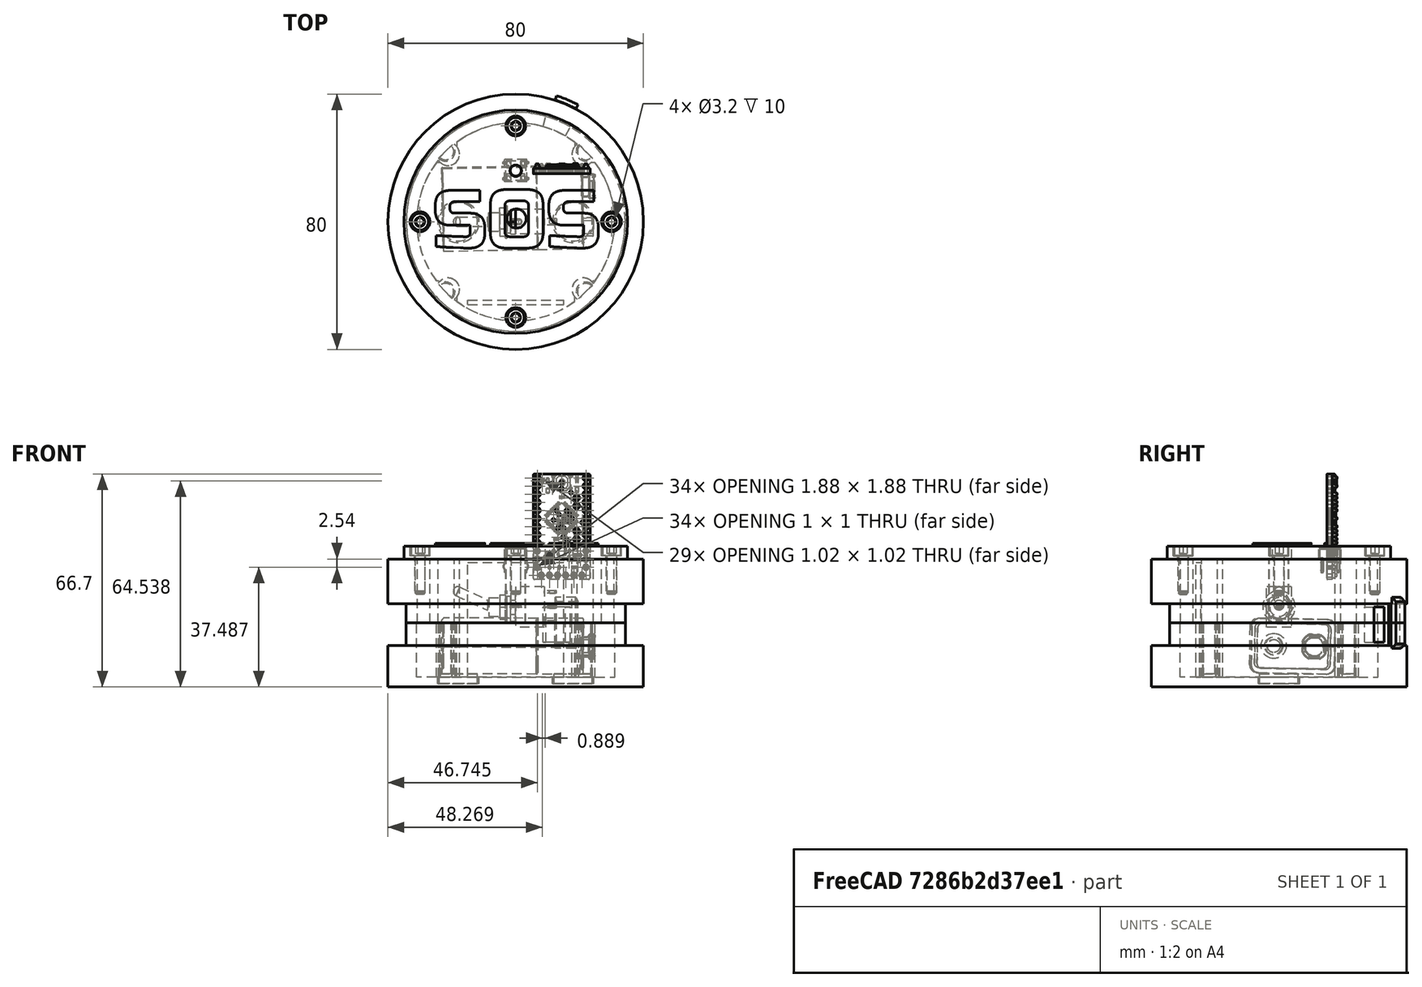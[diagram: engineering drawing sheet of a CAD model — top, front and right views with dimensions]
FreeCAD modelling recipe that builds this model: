
FCSTD DOCUMENT  (FreeCAD 0.17R12852 (Git))
Label: baliza_SOS_vial
License: All rights reserved
LicenseURL: http://es.wikipedia.org/wiki/Todos_los_derechos_reservados
objects: Part::Feature×162, Part::Cylinder×53, App::Part×20, Part::MultiFuse×18, Part::Cut×17, Part::Chamfer×7, Part::Box×2, App::DocumentObjectGroup×2, Part::Part2DObjectPython×1, Part::Extrusion×1, Part::Compound×1
note: 262 computed .brp shape members not serialized (recipe doc carries the construction recipe); baked Part::Feature solids carry a one-line shape summary decoded from their .brp

FEATURE [Part::Feature] Part__Feature  label="BAT 9v"
  Placement = pos=(65.8799,25.4256,-21.3482) rot=(-0.007455,0.009989,0.999922;1.58855rad)
  shape: bbox 48.07 x 27.42 x 18.05 mm, 192 faces (baked)
FEATURE [Part::Cylinder] Cylinder  label="exterior"
  Angle = 360
  AttacherType = Attacher::AttachEngine3D
  Height = 20
  Placement = pos=(0,0,-25) rot=(0,0,1;0rad)
  Radius = 40
FEATURE [Part::Cylinder] Cylinder001  label="vaciado"
  Angle = 360
  AttacherType = Attacher::AttachEngine3D
  Height = 20
  Placement = pos=(0,0,-22) rot=(0,0,1;0rad)
  Radius = 31
FEATURE [Part::Cylinder] Cylinder002  label="tira led exterior"
  Angle = 360
  AttacherType = Attacher::AttachEngine3D
  Height = 13
  Placement = pos=(0,0,-25) rot=(0,0,1;0rad)
  Radius = 41
FEATURE [Part::Cylinder] Cylinder003  label="tira led vaciado"
  Angle = 360
  AttacherType = Attacher::AttachEngine3D
  Height = 13
  Placement = pos=(0,0,-25) rot=(0,0,1;0rad)
  Radius = 34.3
FEATURE [Part::Cylinder] Cylinder004  label="orificio entrada cables sup"
  Angle = 14
  AttacherType = Attacher::AttachEngine3D
  Height = 11
  Placement = pos=(0,0,-11) rot=(0,0,1;1.0472rad)
  Radius = 35
FEATURE [Part::Chamfer] Chamfer001  label="M3 10mm004"
  Edges = 2 edges r=0.1: [Edge6,Edge7]
  Placement = pos=(0,-30,16) rot=(0,0,1;0rad)
FEATURE [Part::Cylinder] Cylinder010  label="torre tornillo003"
  Angle = 360
  AttacherType = Attacher::AttachEngine3D
  Height = 20
  Placement = pos=(0,-30,-25) rot=(0,0,1;0rad)
  Radius = 3.1
FEATURE [Part::Cylinder] Cylinder011  label="torre tornillo002"
  Angle = 360
  AttacherType = Attacher::AttachEngine3D
  Height = 20
  Placement = pos=(30,0,-25) rot=(0,0,1;0rad)
  Radius = 3.1
FEATURE [Part::Cylinder] Cylinder012  label="torre tornillo001"
  Angle = 360
  AttacherType = Attacher::AttachEngine3D
  Height = 20
  Placement = pos=(-30,0,-25) rot=(0,0,1;0rad)
  Radius = 3.1
FEATURE [Part::Cylinder] Cylinder013  label="torre tornillo"
  Angle = 360
  AttacherType = Attacher::AttachEngine3D
  Height = 20
  Placement = pos=(0,30,-25) rot=(0,0,1;0rad)
  Radius = 3.1
FEATURE [Part::Cylinder] Cylinder014  label="orificio tornillo"
  Angle = 360
  AttacherType = Attacher::AttachEngine3D
  Height = 10
  Placement = pos=(0,-30,5) rot=(0,0,1;0rad)
  Radius = 1.6
FEATURE [Part::Cylinder] Cylinder015  label="orificio tornillo001"
  Angle = 360
  AttacherType = Attacher::AttachEngine3D
  Height = 10
  Placement = pos=(-30,0,5) rot=(0,0,1;0rad)
  Radius = 1.6
FEATURE [Part::Cylinder] Cylinder016  label="orificio tornillo002"
  Angle = 360
  AttacherType = Attacher::AttachEngine3D
  Height = 10
  Placement = pos=(30,0,5) rot=(0,0,1;0rad)
  Radius = 1.6
FEATURE [Part::Cylinder] Cylinder017  label="orificio tornillo003"
  Angle = 360
  AttacherType = Attacher::AttachEngine3D
  Height = 10
  Placement = pos=(0,30,5) rot=(0,0,1;0rad)
  Radius = 1.6
FEATURE [Part::MultiFuse] Fusion  label="torres superiores"
  Placement = pos=(0,0,20) rot=(0,0,1;0rad)
  Shapes = -> [Cylinder010,Cylinder012,Cylinder013,Cylinder011]
FEATURE [Part::MultiFuse] Fusion017  label="orificios tornillos"
  Shapes = -> [Cylinder014,Cylinder016,Cylinder015,Cylinder017]
FEATURE [Part::Cylinder] Cylinder018  label="neodimio"
  Angle = 360
  AttacherType = Attacher::AttachEngine3D
  Height = 3
  Placement = pos=(18,0,-24) rot=(0,0,1;0.017453rad)
  Radius = 6
FEATURE [Part::Cylinder] Cylinder019  label="neodimio001"
  Angle = 360
  AttacherType = Attacher::AttachEngine3D
  Height = 3
  Placement = pos=(-18,0,-24) rot=(0,0,1;0.017453rad)
  Radius = 6
FEATURE [Part::Cylinder] Cylinder020  label="base neodimio002"
  Angle = 360
  AttacherType = Attacher::AttachEngine3D
  Height = 3
  Placement = pos=(18,0,-24) rot=(0,0,1;0.017453rad)
  Radius = 6.5
FEATURE [Part::Cylinder] Cylinder021  label="base neodimio003"
  Angle = 360
  AttacherType = Attacher::AttachEngine3D
  Height = 3
  Placement = pos=(-18,0,-24) rot=(0,0,1;0.017453rad)
  Radius = 6.5
FEATURE [Part::MultiFuse] Fusion018  label="bases neodimio"
  Shapes = -> [Cylinder020,Cylinder021]
FEATURE [Part::MultiFuse] Fusion019  label="Neodimios"
  Shapes = -> [Cylinder018,Cylinder019]
FEATURE [Part::Feature] Part__Feature001  label="Small Toggle Switch"
  shape: bbox 11.9 x 2.92 x 7.366 mm, 3 faces (baked)
FEATURE [Part::Feature] Part__Feature002  label="Small Toggle Switch001"
  shape: bbox 21.22 x 10.16 x 12.7 mm, 53 faces (baked)
FEATURE [App::Part] Small_Toggle_Switch
  Group = -> [Part__Feature001,Part__Feature002]
  License = CC BY 3.0
  LicenseURL = http://creativecommons.org/licenses/by/3.0/
  Origin = -> Origin
  Placement = pos=(0.25,1,17) rot=(0,1,0;1.5708rad)
FEATURE [Part::Cut] Cut  label="caja parte inferior"
  Base = -> Cylinder
  Tool = -> Cylinder001
FEATURE [Part::Cylinder] Cylinder027  label="exterior003"
  Angle = 360
  AttacherType = Attacher::AttachEngine3D
  Height = 20
  Placement = pos=(0,0,-25) rot=(0,0,1;0rad)
  Radius = 40
FEATURE [Part::Cylinder] Cylinder028  label="vaciado001"
  Angle = 360
  AttacherType = Attacher::AttachEngine3D
  Height = 20
  Placement = pos=(0,0,-25) rot=(0,0,1;0rad)
  Radius = 31
FEATURE [Part::Cut] Cut009  label="caja parte superior"
  Base = -> Cylinder027
  Placement = pos=(0,0,20) rot=(0,0,1;0rad)
  Tool = -> Cylinder028
FEATURE [Part::Cylinder] Cylinder029  label="torre fijacion001"
  Angle = 360
  AttacherType = Attacher::AttachEngine3D
  Height = 20
  Placement = pos=(0,-30,-25) rot=(0,0,1;0rad)
  Radius = 3.6
FEATURE [Part::Cylinder] Cylinder030  label="torre fijacion004"
  Angle = 360
  AttacherType = Attacher::AttachEngine3D
  Height = 20
  Placement = pos=(30,0,-25) rot=(0,0,1;0rad)
  Radius = 3.6
FEATURE [Part::Cylinder] Cylinder031  label="torre fijacion002"
  Angle = 360
  AttacherType = Attacher::AttachEngine3D
  Height = 20
  Placement = pos=(-30,0,-25) rot=(0,0,1;0rad)
  Radius = 3.6
FEATURE [Part::Cylinder] Cylinder032  label="torre fijacion003"
  Angle = 360
  AttacherType = Attacher::AttachEngine3D
  Height = 20
  Placement = pos=(0,30,-25) rot=(0,0,1;0rad)
  Radius = 3.6
FEATURE [Part::MultiFuse] Fusion023  label="torres inferiores"
  Placement = pos=(0,0,0) rot=(0,0,1;0.785398rad)
  Shapes = -> [Cylinder029,Cylinder031,Cylinder032,Cylinder030]
FEATURE [Part::Cut] Cut010  label="vaciado tira led inf"
  Base = -> Cylinder002
  Placement = pos=(0,0,13) rot=(0,0,1;0rad)
  Tool = -> Cylinder003
FEATURE [Part::Cylinder] Cylinder035  label="tira led exterior001"
  Angle = 360
  AttacherType = Attacher::AttachEngine3D
  Height = 13
  Placement = pos=(0,0,-25) rot=(0,0,1;0rad)
  Radius = 41
FEATURE [Part::Cylinder] Cylinder036  label="tira led vaciado001"
  Angle = 360
  AttacherType = Attacher::AttachEngine3D
  Height = 13
  Placement = pos=(0,0,-25) rot=(0,0,1;0rad)
  Radius = 34.3
FEATURE [Part::Cut] Cut013  label="vaciado tira led sup"
  Base = -> Cylinder035
  Placement = pos=(0,0,13) rot=(0,0,1;0rad)
  Tool = -> Cylinder036
FEATURE [Part::Cut] Cut014  label="caja parte superior001"
  Base = -> Cut009
  Tool = -> Cut013
FEATURE [Part::Cut] Cut015  label="caja parte inferior001"
  Base = -> Cut
  Tool = -> Cut010
FEATURE [Part::Cylinder] Cylinder037  label="vaciado fijacion001"
  Angle = 180
  AttacherType = Attacher::AttachEngine3D
  Height = 20
  Placement = pos=(0,-31,-25) rot=(0,0,1;0rad)
  Radius = 3
FEATURE [Part::Cylinder] Cylinder038  label="vaciado fijacion004"
  Angle = 180
  AttacherType = Attacher::AttachEngine3D
  Height = 20
  Placement = pos=(31.061,0.06103,-25) rot=(0,0,1;1.5708rad)
  Radius = 3
FEATURE [Part::Cylinder] Cylinder039  label="vaciado fijacion002"
  Angle = 180
  AttacherType = Attacher::AttachEngine3D
  Height = 20
  Placement = pos=(-31.0604,0.0980594,-25) rot=(0,0,-1;1.6057rad)
  Radius = 3
FEATURE [Part::Cylinder] Cylinder040  label="vaciado fijacion003"
  Angle = 180
  AttacherType = Attacher::AttachEngine3D
  Height = 20
  Placement = pos=(0,31.122,-25) rot=(0,0,1;-3.14159rad)
  Radius = 3
FEATURE [Part::MultiFuse] Fusion024  label="vaciado fijaciones"
  Placement = pos=(0,0,3) rot=(0,0,1;0.785398rad)
  Shapes = -> [Cylinder037,Cylinder039,Cylinder040,Cylinder038]
FEATURE [Part::Cylinder] Cylinder041  label="fijacion001"
  Angle = 180
  AttacherType = Attacher::AttachEngine3D
  Height = 20
  Placement = pos=(0,-31,-25) rot=(0,0,1;0rad)
  Radius = 2.6
FEATURE [Part::Cylinder] Cylinder042  label="fijacion002"
  Angle = 180
  AttacherType = Attacher::AttachEngine3D
  Height = 20
  Placement = pos=(-31.0604,0.0980594,-25) rot=(0,0,-1;1.6057rad)
  Radius = 2.6
FEATURE [Part::Cylinder] Cylinder043  label="fijacion003"
  Angle = 180
  AttacherType = Attacher::AttachEngine3D
  Height = 20
  Placement = pos=(0,31.122,-25) rot=(0,0,1;-3.14159rad)
  Radius = 2.6
FEATURE [Part::Cylinder] Cylinder044  label="fijacion004"
  Angle = 180
  AttacherType = Attacher::AttachEngine3D
  Height = 20
  Placement = pos=(31.061,0.06103,-25) rot=(0,0,1;1.5708rad)
  Radius = 2.6
FEATURE [Part::MultiFuse] Fusion025  label="fijaciones superior_inferior"
  Placement = pos=(0,0,4) rot=(0,0,1;0.785398rad)
  Shapes = -> [Cylinder041,Cylinder042,Cylinder043,Cylinder044]
FEATURE [Part::MultiFuse] Fusion026
  Shapes = -> [Cut015,Fusion023]
FEATURE [Part::Cut] Cut016  label="parte inferior"
  Base = -> Fusion026
  Tool = -> Fusion024
FEATURE [Part::Cylinder] Cylinder045  label="torre tornillo016"
  Angle = 360
  AttacherType = Attacher::AttachEngine3D
  Height = 20
  Placement = pos=(0,-30,-25) rot=(0,0,1;0rad)
  Radius = 3.6
FEATURE [Part::Cylinder] Cylinder046  label="torre tornillo017"
  Angle = 360
  AttacherType = Attacher::AttachEngine3D
  Height = 20
  Placement = pos=(30,0,-25) rot=(0,0,1;0rad)
  Radius = 3.6
FEATURE [Part::Cylinder] Cylinder047  label="torre tornillo018"
  Angle = 360
  AttacherType = Attacher::AttachEngine3D
  Height = 20
  Placement = pos=(-30,0,-25) rot=(0,0,1;0rad)
  Radius = 3.6
FEATURE [Part::Cylinder] Cylinder048  label="torre tornillo019"
  Angle = 360
  AttacherType = Attacher::AttachEngine3D
  Height = 20
  Placement = pos=(0,30,-25) rot=(0,0,1;0rad)
  Radius = 3.6
FEATURE [Part::MultiFuse] Fusion027  label="torres superiores001"
  Placement = pos=(0,0,20) rot=(0,0,1;0.785398rad)
  Shapes = -> [Cylinder045,Cylinder047,Cylinder048,Cylinder046]
FEATURE [Part::MultiFuse] Fusion028
  Shapes = -> [Cut014,Fusion027]
FEATURE [Part::MultiFuse] Fusion029  label="parte superior fijaciones inferiores"
  Shapes = -> [Fusion025,Fusion028]
FEATURE [Part::MultiFuse] Fusion030
  Shapes = -> [Fusion,Fusion029]
FEATURE [Part::Cut] Cut017  label="parte superior"
  Base = -> Fusion030
  Tool = -> Fusion017
FEATURE [Part::Cut] Cut018  label="parte inferior001"
  Base = -> Cut016
  Tool = -> Fusion018
FEATURE [Part::Cylinder] Cylinder049  label="orificio entrada cables inf"
  Angle = 14
  AttacherType = Attacher::AttachEngine3D
  Height = 11
  Placement = pos=(0,0,-11) rot=(0,0,1;1.0472rad)
  Radius = 35
FEATURE [Part::Cut] Cut019  label="parte inferior v1"
  Base = -> Cut018
  Tool = -> Cylinder049
FEATURE [Part::Cut] Cut020  label="parte superior001"
  Base = -> Cut017
  Tool = -> Cylinder004
FEATURE [Part::Cylinder] Cylinder052  label="tapa superior"
  Angle = 360
  AttacherType = Attacher::AttachEngine3D
  Height = 4
  Placement = pos=(0,0,15) rot=(0,0,1;0rad)
  Radius = 35
FEATURE [Part::Cylinder] Cylinder053  label="entrada tornillo004"
  Angle = 360
  AttacherType = Attacher::AttachEngine3D
  Height = 3
  Placement = pos=(0,-30,16) rot=(0,0,1;0rad)
  Radius = 3.1
FEATURE [Part::Cylinder] Cylinder054  label="entrada tornillo005"
  Angle = 360
  AttacherType = Attacher::AttachEngine3D
  Height = 3
  Placement = pos=(0,30,16) rot=(0,0,1;0rad)
  Radius = 3.1
FEATURE [Part::Cylinder] Cylinder055  label="entrada tornillo006"
  Angle = 360
  AttacherType = Attacher::AttachEngine3D
  Height = 3
  Placement = pos=(30,0,16) rot=(0,0,1;0rad)
  Radius = 3.1
FEATURE [Part::Cylinder] Cylinder056  label="entrada tornillo007"
  Angle = 360
  AttacherType = Attacher::AttachEngine3D
  Height = 3
  Placement = pos=(-30,0,16) rot=(0,0,1;0rad)
  Radius = 3.1
FEATURE [Part::MultiFuse] Fusion036  label="vaciados cabeza tornillos001"
  Shapes = -> [Cylinder053,Cylinder055,Cylinder056,Cylinder054]
FEATURE [Part::Cut] Cut006
  Base = -> Cylinder052
  Tool = -> Fusion036
FEATURE [Part::Cylinder] Cylinder057  label="orificio tornillo008"
  Angle = 360
  AttacherType = Attacher::AttachEngine3D
  Height = 10
  Placement = pos=(0,-30,5) rot=(0,0,1;0rad)
  Radius = 1.7
FEATURE [Part::Cylinder] Cylinder058  label="orificio tornillo009"
  Angle = 360
  AttacherType = Attacher::AttachEngine3D
  Height = 10
  Placement = pos=(30,0,5) rot=(0,0,1;0rad)
  Radius = 1.7
FEATURE [Part::Cylinder] Cylinder059  label="orificio tornillo010"
  Angle = 360
  AttacherType = Attacher::AttachEngine3D
  Height = 10
  Placement = pos=(-30,0,5) rot=(0,0,1;0rad)
  Radius = 1.7
FEATURE [Part::Cylinder] Cylinder060  label="orificio tornillo011"
  Angle = 360
  AttacherType = Attacher::AttachEngine3D
  Height = 10
  Placement = pos=(0,30,5) rot=(0,0,1;0rad)
  Radius = 1.7
FEATURE [Part::MultiFuse] Fusion037  label="orificios tornillos002"
  Placement = pos=(0,0,3) rot=(0,0,1;0rad)
  Shapes = -> [Cylinder057,Cylinder058,Cylinder059,Cylinder060]
FEATURE [Part::Cut] Cut007  label="tapa superior001"
  Base = -> Cut006
  Tool = -> Fusion037
FEATURE [Part::Part2DObjectPython] ShapeString001  # Draft 2D object (typed FeaturePython)
  FontFile = <userpath>/Descargas/Russo_One/RussoOne-Regular.ttf
  Placement = pos=(-26,-8,19) rot=(0,0,1;0rad)
  Size = 10
  String = SOS
  Tracking = 0
FEATURE [Part::Extrusion] Extrude002
  Base = -> ShapeString001
  Dir = (0,0,1)
  DirMode = 2
  FaceMakerClass = Part::FaceMakerBullseye
  LengthFwd = 1
  LengthRev = 0
  Solid = true
  Symmetric = false
FEATURE [Part::MultiFuse] Fusion022  label="tapa"
  Shapes = -> [Extrude002,Cut007]
FEATURE [Part::Cylinder] Cylinder061  label="Cilindro001"
  Angle = 360
  AttacherType = Attacher::AttachEngine3D
  Height = 10
  Placement = pos=(0.25,1,11) rot=(0,0,1;0rad)
  Radius = 3
FEATURE [Part::Cut] Cut008  label="tapa interruptor sin pushbutton"
  Base = -> Fusion022
  Tool = -> Cylinder061
FEATURE [Part::Feature] Part__Feature003  label="board"
  Placement = pos=(5.47521,15.0552,41.6975) rot=(0,0,1;0rad)
  shape: bbox 17.85 x 1.67 x 33.09 mm, 530 faces (baked)
FEATURE [Part::Feature] Part__Feature004  label="ATmega"
  Placement = pos=(14.3652,16.8027,27.7275) rot=(0,-1,0;0.785398rad)
  shape: bbox 10.57 x 1.099 x 10.57 mm, 1762 faces (baked)
FEATURE [Part::Feature] Part__Feature005  label="cap_603"
  Placement = pos=(10.3417,16.7052,40.4401) rot=(0,1,0;1.5708rad)
  shape: bbox 0.8 x 0.8 x 0.4 mm, 18 faces (baked)
FEATURE [Part::Feature] Part__Feature006  label="cap_604"
  Placement = pos=(10.3417,16.7052,40.4401) rot=(0,1,0;1.5708rad)
  shape: bbox 0.8 x 0.8 x 0.4 mm, 18 faces (baked)
FEATURE [Part::Feature] Part__Feature007  label="cap_605"
  Placement = pos=(10.3417,16.7052,40.4401) rot=(0,1,0;1.5708rad)
  shape: bbox 0.8 x 0.8 x 0.8 mm, 10 faces (baked)
FEATURE [App::Part] cap_603  label="cap_606"
  Group = -> [Part__Feature005,Part__Feature006,Part__Feature007]
  License = CC BY 3.0
  LicenseURL = http://creativecommons.org/licenses/by/3.0/
  Origin = -> Origin001
FEATURE [Part::Feature] Part__Feature008  label="cap_607"
  Placement = pos=(13.6922,16.7052,34.8585) rot=(0,0,1;0rad)
  shape: bbox 0.4 x 0.8 x 0.8 mm, 18 faces (baked)
FEATURE [Part::Feature] Part__Feature009  label="cap_608"
  Placement = pos=(13.6922,16.7052,34.8585) rot=(0,0,1;0rad)
  shape: bbox 0.4 x 0.8 x 0.8 mm, 18 faces (baked)
FEATURE [Part::Feature] Part__Feature010  label="cap_609"
  Placement = pos=(13.6922,16.7052,34.8585) rot=(0,0,1;0rad)
  shape: bbox 0.8 x 0.8 x 0.8 mm, 10 faces (baked)
FEATURE [App::Part] cap_603001
  Group = -> [Part__Feature008,Part__Feature009,Part__Feature010]
  License = CC BY 3.0
  LicenseURL = http://creativecommons.org/licenses/by/3.0/
  Origin = -> Origin002
FEATURE [Part::Feature] Part__Feature011  label="cap_603002"
  Placement = pos=(11.8634,16.7052,21.6759) rot=(0,0,1;0rad)
  shape: bbox 0.4 x 0.8 x 0.8 mm, 18 faces (baked)
FEATURE [Part::Feature] Part__Feature012  label="cap_603003"
  Placement = pos=(11.8634,16.7052,21.6759) rot=(0,0,1;0rad)
  shape: bbox 0.4 x 0.8 x 0.8 mm, 18 faces (baked)
FEATURE [Part::Feature] Part__Feature013  label="cap_603004"
  Placement = pos=(11.8634,16.7052,21.6759) rot=(0,0,1;0rad)
  shape: bbox 0.8 x 0.8 x 0.8 mm, 10 faces (baked)
FEATURE [App::Part] cap_603002  label="cap_603005"
  Group = -> [Part__Feature011,Part__Feature012,Part__Feature013]
  License = CC BY 3.0
  LicenseURL = http://creativecommons.org/licenses/by/3.0/
  Origin = -> Origin003
FEATURE [Part::Feature] Part__Feature014  label="cap_603006"
  Placement = pos=(17.4768,16.7052,12.8875) rot=(0,0,1;0rad)
  shape: bbox 0.4 x 0.8 x 0.8 mm, 18 faces (baked)
FEATURE [Part::Feature] Part__Feature015  label="cap_603007"
  Placement = pos=(17.4768,16.7052,12.8875) rot=(0,0,1;0rad)
  shape: bbox 0.4 x 0.8 x 0.8 mm, 18 faces (baked)
FEATURE [Part::Feature] Part__Feature016  label="cap_603008"
  Placement = pos=(17.4768,16.7052,12.8875) rot=(0,0,1;0rad)
  shape: bbox 0.8 x 0.8 x 0.8 mm, 10 faces (baked)
FEATURE [App::Part] cap_603003  label="cap_603009"
  Group = -> [Part__Feature014,Part__Feature015,Part__Feature016]
  License = CC BY 3.0
  LicenseURL = http://creativecommons.org/licenses/by/3.0/
  Origin = -> Origin004
FEATURE [Part::Feature] Part__Feature017  label="res_603"
  Placement = pos=(10.4218,16.7052,37.2651) rot=(0,1,0;1.5708rad)
  shape: bbox 0.8 x 0.5 x 0.3 mm, 18 faces (baked)
FEATURE [Part::Feature] Part__Feature018  label="res_604"
  Placement = pos=(10.4218,16.7052,37.2651) rot=(0,1,0;1.5708rad)
  shape: bbox 0.8 x 0.5 x 0.3 mm, 18 faces (baked)
FEATURE [Part::Feature] Part__Feature019  label="res_605"
  Placement = pos=(10.4218,16.7052,37.2651) rot=(0,1,0;1.5708rad)
  shape: bbox 0.8 x 0.5 x 1 mm, 10 faces (baked)
FEATURE [App::Part] res_603  label="res_606"
  Group = -> [Part__Feature017,Part__Feature018,Part__Feature019]
  License = CC BY 3.0
  LicenseURL = http://creativecommons.org/licenses/by/3.0/
  Origin = -> Origin005
FEATURE [Part::Feature] Part__Feature020  label="res_607"
  Placement = pos=(19.5912,16.7052,37.5953) rot=(0,1,0;1.5708rad)
  shape: bbox 0.8 x 0.5 x 0.3 mm, 18 faces (baked)
FEATURE [Part::Feature] Part__Feature021  label="res_608"
  Placement = pos=(19.5912,16.7052,37.5953) rot=(0,1,0;1.5708rad)
  shape: bbox 0.8 x 0.5 x 0.3 mm, 18 faces (baked)
FEATURE [Part::Feature] Part__Feature022  label="res_609"
  Placement = pos=(19.5912,16.7052,37.5953) rot=(0,1,0;1.5708rad)
  shape: bbox 0.8 x 0.5 x 1 mm, 10 faces (baked)
FEATURE [App::Part] res_603001
  Group = -> [Part__Feature020,Part__Feature021,Part__Feature022]
  License = CC BY 3.0
  LicenseURL = http://creativecommons.org/licenses/by/3.0/
  Origin = -> Origin006
FEATURE [Part::Feature] Part__Feature023  label="res_603002"
  Placement = pos=(15.1652,16.7052,14.6275) rot=(0,1,0;-3.14159rad)
  shape: bbox 0.3 x 0.5 x 0.8 mm, 18 faces (baked)
FEATURE [Part::Feature] Part__Feature024  label="res_603003"
  Placement = pos=(15.1652,16.7052,14.6275) rot=(0,1,0;-3.14159rad)
  shape: bbox 0.3 x 0.5 x 0.8 mm, 18 faces (baked)
FEATURE [Part::Feature] Part__Feature025  label="res_603004"
  Placement = pos=(15.1652,16.7052,14.6275) rot=(0,1,0;-3.14159rad)
  shape: bbox 1 x 0.5 x 0.8 mm, 10 faces (baked)
FEATURE [App::Part] res_603002  label="res_603005"
  Group = -> [Part__Feature023,Part__Feature024,Part__Feature025]
  License = CC BY 3.0
  LicenseURL = http://creativecommons.org/licenses/by/3.0/
  Origin = -> Origin007
FEATURE [Part::Feature] Part__Feature026  label="condensateurTantale_106C_Dfaut"
  Placement = pos=(10.1742,17.5052,15.6625) rot=(0,1,0;1.5708rad)
  shape: bbox 1.2 x 0.8101 x 0.6565 mm, 50 faces (baked)
FEATURE [Part::Feature] Part__Feature027  label="condensateurTantale_106C_Dfaut001"
  Placement = pos=(10.1742,17.5052,15.6625) rot=(0,1,0;1.5708rad)
  shape: bbox 1.2 x 0.8101 x 0.6565 mm, 50 faces (baked)
FEATURE [Part::Feature] Part__Feature028  label="condensateurTantale_106C_Dfaut002"
  Placement = pos=(10.1742,17.5052,15.6625) rot=(0,1,0;1.5708rad)
  shape: bbox 1.6 x 1.551 x 3.187 mm, 88 faces (baked)
FEATURE [App::Part] condensateurTantale_106C_D__faut
  Group = -> [Part__Feature026,Part__Feature027,Part__Feature028]
  License = CC BY 3.0
  LicenseURL = http://creativecommons.org/licenses/by/3.0/
  Origin = -> Origin008
FEATURE [Part::Feature] Part__Feature029  label="condensateurTantale_106C_Dfaut003"
  Placement = pos=(18.6832,17.5052,17.5675) rot=(0,1,0;1.5708rad)
  shape: bbox 1.2 x 0.8101 x 0.6565 mm, 50 faces (baked)
FEATURE [Part::Feature] Part__Feature030  label="condensateurTantale_106C_Dfaut004"
  Placement = pos=(18.6832,17.5052,17.5675) rot=(0,1,0;1.5708rad)
  shape: bbox 1.2 x 0.8101 x 0.6565 mm, 50 faces (baked)
FEATURE [Part::Feature] Part__Feature031  label="condensateurTantale_106C_Dfaut005"
  Placement = pos=(18.6832,17.5052,17.5675) rot=(0,1,0;1.5708rad)
  shape: bbox 1.6 x 1.551 x 3.187 mm, 88 faces (baked)
FEATURE [App::Part] condensateurTantale_106C_D__faut001
  Group = -> [Part__Feature029,Part__Feature030,Part__Feature031]
  License = CC BY 3.0
  LicenseURL = http://creativecommons.org/licenses/by/3.0/
  Origin = -> Origin009
FEATURE [Part::Feature] Part__Feature032  label="SOT23-5"
  Placement = pos=(14.3653,16.6848,17.5167) rot=(-1,0,0;1.5708rad)
  shape: bbox 0.6498 x 0.8924 x 0.5 mm, 7 faces (baked)
FEATURE [Part::Feature] Part__Feature033  label="SOT23-006"
  Placement = pos=(14.3653,16.6848,17.5167) rot=(-1,0,0;1.5708rad)
  shape: bbox 1.823 x 2.71 x 3.209 mm, 34 faces (baked)
FEATURE [Part::Feature] Part__Feature034  label="SOT23-007"
  Placement = pos=(14.3653,16.6848,17.5167) rot=(-1,0,0;1.5708rad)
  shape: bbox 0.6498 x 0.8924 x 0.5 mm, 7 faces (baked)
FEATURE [Part::Feature] Part__Feature035  label="SOT23-008"
  Placement = pos=(14.3653,16.6848,17.5167) rot=(-1,0,0;1.5708rad)
  shape: bbox 0.6498 x 0.8924 x 0.5 mm, 7 faces (baked)
FEATURE [Part::Feature] Part__Feature036  label="SOT23-009"
  Placement = pos=(14.3653,16.6848,17.5167) rot=(-1,0,0;1.5708rad)
  shape: bbox 0.6498 x 0.8924 x 0.5 mm, 7 faces (baked)
FEATURE [Part::Feature] Part__Feature037  label="SOT23-010"
  Placement = pos=(14.3653,16.6848,17.5167) rot=(-1,0,0;1.5708rad)
  shape: bbox 0.6498 x 0.8924 x 0.5 mm, 7 faces (baked)
FEATURE [App::Part] SOT23_5
  Group = -> [Part__Feature032,Part__Feature033,Part__Feature034,Part__Feature035,Part__Feature036,Part__Feature037]
  License = CC BY 3.0
  LicenseURL = http://creativecommons.org/licenses/by/3.0/
  Origin = -> Origin010
FEATURE [Part::Feature] Part__Feature038  label="Surface Mount Chip LED 3.2x1.6mm"
  Placement = pos=(18.7112,16.7112,39.0103) rot=(0.57735,0.57735,0.57735;-2.0944rad)
  shape: bbox 0.96 x 0.006 x 0.24 mm, 10 faces (baked)
FEATURE [Part::Feature] Part__Feature039  label="Surface Mount Chip LED 3.2x1.6mm001"
  Placement = pos=(18.7112,16.7112,39.0103) rot=(0.57735,0.57735,0.57735;-2.0944rad)
  shape: bbox 0.72 x 0.312 x 0.36 mm, 15 faces (baked)
FEATURE [Part::Feature] Part__Feature040  label="Surface Mount Chip LED 3.2x1.6mm002"
  Placement = pos=(18.7112,16.7112,39.0103) rot=(0.57735,0.57735,0.57735;-2.0944rad)
  shape: bbox 0.96 x 0.3661 x 1.2 mm, 24 faces (baked)
FEATURE [Part::Feature] Part__Feature041  label="Surface Mount Chip LED 3.2x1.6mm003"
  Placement = pos=(18.7112,16.7112,39.0103) rot=(0.57735,0.57735,0.57735;-2.0944rad)
  shape: bbox 0.72 x 0.312 x 0.36 mm, 17 faces (baked)
FEATURE [Part::Feature] Part__Feature042  label="Surface Mount Chip LED 3.2x1.6mm004"
  Placement = pos=(18.7112,16.7112,39.0103) rot=(0.57735,0.57735,0.57735;-2.0944rad)
  shape: bbox 0.984 x 0.36 x 1.944 mm, 79 faces (baked)
FEATURE [Part::Feature] Part__Feature043  label="Surface Mount Chip LED 3.2x1.6mm005"
  Placement = pos=(18.7112,16.7112,39.0103) rot=(0.57735,0.57735,0.57735;-2.0944rad)
  shape: bbox 0.12 x 0.006 x 0.12 mm, 6 faces (baked)
FEATURE [Part::Feature] Part__Feature044  label="Surface Mount Chip LED 3.2x1.6mm006"
  Placement = pos=(18.7112,16.7112,39.0103) rot=(0.57735,0.57735,0.57735;-2.0944rad)
  shape: bbox 0.12 x 0.006 x 0.12 mm, 6 faces (baked)
FEATURE [App::Part] Surface_Mount_Chip_LED_3_2x1_6mm
  Group = -> [Part__Feature038,Part__Feature039,Part__Feature040,Part__Feature041,Part__Feature042,Part__Feature043,Part__Feature044]
  License = CC BY 3.0
  LicenseURL = http://creativecommons.org/licenses/by/3.0/
  Origin = -> Origin011
FEATURE [Part::Feature] Part__Feature045  label="Surface Mount Chip LED 3.2x1.6mm007"
  Placement = pos=(13.4306,16.7112,20.3081) rot=(-1,0,0;1.5708rad)
  shape: bbox 0.24 x 0.006 x 0.96 mm, 10 faces (baked)
FEATURE [Part::Feature] Part__Feature046  label="Surface Mount Chip LED 3.2x1.6mm008"
  Placement = pos=(13.4306,16.7112,20.3081) rot=(-1,0,0;1.5708rad)
  shape: bbox 0.36 x 0.312 x 0.72 mm, 15 faces (baked)
FEATURE [Part::Feature] Part__Feature047  label="Surface Mount Chip LED 3.2x1.6mm009"
  Placement = pos=(13.4306,16.7112,20.3081) rot=(-1,0,0;1.5708rad)
  shape: bbox 1.2 x 0.3661 x 0.96 mm, 24 faces (baked)
FEATURE [Part::Feature] Part__Feature048  label="Surface Mount Chip LED 3.2x1.6mm010"
  Placement = pos=(13.4306,16.7112,20.3081) rot=(-1,0,0;1.5708rad)
  shape: bbox 0.36 x 0.312 x 0.72 mm, 17 faces (baked)
FEATURE [Part::Feature] Part__Feature049  label="Surface Mount Chip LED 3.2x1.6mm011"
  Placement = pos=(13.4306,16.7112,20.3081) rot=(-1,0,0;1.5708rad)
  shape: bbox 1.944 x 0.36 x 0.984 mm, 79 faces (baked)
FEATURE [Part::Feature] Part__Feature050  label="Surface Mount Chip LED 3.2x1.6mm012"
  Placement = pos=(13.4306,16.7112,20.3081) rot=(-1,0,0;1.5708rad)
  shape: bbox 0.12 x 0.006 x 0.12 mm, 6 faces (baked)
FEATURE [Part::Feature] Part__Feature051  label="Surface Mount Chip LED 3.2x1.6mm013"
  Placement = pos=(13.4306,16.7112,20.3081) rot=(-1,0,0;1.5708rad)
  shape: bbox 0.12 x 0.006 x 0.12 mm, 6 faces (baked)
FEATURE [App::Part] Surface_Mount_Chip_LED_3_2x1_6mm001
  Group = -> [Part__Feature045,Part__Feature046,Part__Feature047,Part__Feature048,Part__Feature049,Part__Feature050,Part__Feature051]
  License = CC BY 3.0
  LicenseURL = http://creativecommons.org/licenses/by/3.0/
  Origin = -> Origin012
FEATURE [Part::Feature] Part__Feature052  label="Fusion001"
  shape: bbox 5.215 x 3.028 x 0.825 mm, 41 faces (baked)
FEATURE [App::Part] Crystal_Low_Profile
  Group = -> [Part__Feature052]
  License = CC BY 3.0
  LicenseURL = http://creativecommons.org/licenses/by/3.0/
  Origin = -> Origin013
  Placement = pos=(9.71701,16.7052,22.6754) rot=(-0.57735,0.57735,0.57735;2.0944rad)
FEATURE [Part::Feature] Part__Feature053  label="TACTILE-SWITCH-SMD-ALT01"
  Placement = pos=(14.4922,16.7052,39.0305) rot=(0,0,1;0rad)
  shape: bbox 6.4 x 1.404 x 5.219 mm, 156 faces (baked)
FEATURE [Part::Feature] Part__Feature054  label="Pin Header 1x12 TH Pitch 2.54mm"
  Placement = pos=(6.74521,15.0555,40.428) rot=(0.577364,0.577364,-0.577322;2.09444rad)
  shape: bbox 0.63 x 12.7 x 0.6305 mm, 14 faces, 0 solids (baked)
FEATURE [Part::Feature] Part__Feature055  label="Pin Header 1x12 TH Pitch 2.54mm001"
  Placement = pos=(6.74521,15.0555,40.428) rot=(0.577364,0.577364,-0.577322;2.09444rad)
  shape: bbox 0.63 x 12.7 x 0.6305 mm, 14 faces, 0 solids (baked)
FEATURE [Part::Feature] Part__Feature056  label="Pin Header 1x12 TH Pitch 2.54mm002"
  Placement = pos=(6.74521,15.0555,40.428) rot=(0.577364,0.577364,-0.577322;2.09444rad)
  shape: bbox 0.63 x 12.7 x 0.6305 mm, 14 faces, 0 solids (baked)
FEATURE [Part::Feature] Part__Feature057  label="Pin Header 1x12 TH Pitch 2.54mm003"
  Placement = pos=(6.74521,15.0555,40.428) rot=(0.577364,0.577364,-0.577322;2.09444rad)
  shape: bbox 0.63 x 12.7 x 0.6305 mm, 14 faces, 0 solids (baked)
FEATURE [Part::Feature] Part__Feature058  label="Pin Header 1x12 TH Pitch 2.54mm004"
  Placement = pos=(6.74521,15.0555,40.428) rot=(0.577364,0.577364,-0.577322;2.09444rad)
  shape: bbox 0.63 x 12.7 x 0.6305 mm, 14 faces, 0 solids (baked)
FEATURE [Part::Feature] Part__Feature059  label="Pin Header 1x12 TH Pitch 2.54mm005"
  Placement = pos=(6.74521,15.0555,40.428) rot=(0.577364,0.577364,-0.577322;2.09444rad)
  shape: bbox 0.63 x 12.7 x 0.6305 mm, 14 faces, 0 solids (baked)
FEATURE [Part::Feature] Part__Feature060  label="Pin Header 1x12 TH Pitch 2.54mm006"
  Placement = pos=(6.74521,15.0555,40.428) rot=(0.577364,0.577364,-0.577322;2.09444rad)
  shape: bbox 0.63 x 12.7 x 0.6305 mm, 14 faces, 0 solids (baked)
FEATURE [Part::Feature] Part__Feature061  label="Pin Header 1x12 TH Pitch 2.54mm007"
  Placement = pos=(6.74521,15.0555,40.428) rot=(0.577364,0.577364,-0.577322;2.09444rad)
  shape: bbox 0.63 x 12.7 x 0.6305 mm, 14 faces, 0 solids (baked)
FEATURE [Part::Feature] Part__Feature062  label="Pin Header 1x12 TH Pitch 2.54mm008"
  Placement = pos=(6.74521,15.0555,40.428) rot=(0.577364,0.577364,-0.577322;2.09444rad)
  shape: bbox 0.63 x 12.7 x 0.6305 mm, 14 faces, 0 solids (baked)
FEATURE [Part::Feature] Part__Feature063  label="Pin Header 1x12 TH Pitch 2.54mm009"
  Placement = pos=(6.74521,15.0555,40.428) rot=(0.577364,0.577364,-0.577322;2.09444rad)
  shape: bbox 0.63 x 12.7 x 0.6305 mm, 14 faces, 0 solids (baked)
FEATURE [Part::Feature] Part__Feature064  label="Pin Header 1x12 TH Pitch 2.54mm010"
  Placement = pos=(6.74521,15.0555,40.428) rot=(0.577364,0.577364,-0.577322;2.09444rad)
  shape: bbox 0.63 x 12.7 x 0.6305 mm, 14 faces, 0 solids (baked)
FEATURE [Part::Feature] Part__Feature065  label="Pin Header 1x12 TH Pitch 2.54mm011"
  Placement = pos=(6.74521,15.0555,40.428) rot=(0.577364,0.577364,-0.577322;2.09444rad)
  shape: bbox 0.63 x 12.7 x 0.6305 mm, 14 faces, 0 solids (baked)
FEATURE [Part::Feature] Part__Feature066  label="Pin Header 1x12 TH Pitch 2.54mm012"
  Placement = pos=(6.74521,15.0555,40.428) rot=(0.577364,0.577364,-0.577322;2.09444rad)
  shape: bbox 2.54 x 2.799 x 2.54 mm, 23 faces, 0 solids (baked)
FEATURE [Part::Feature] Part__Feature067  label="Pin Header 1x12 TH Pitch 2.54mm013"
  Placement = pos=(6.74521,15.0555,40.428) rot=(0.577364,0.577364,-0.577322;2.09444rad)
  shape: bbox 2.54 x 2.799 x 2.54 mm, 23 faces, 0 solids (baked)
FEATURE [Part::Feature] Part__Feature068  label="Pin Header 1x12 TH Pitch 2.54mm014"
  Placement = pos=(6.74521,15.0555,40.428) rot=(0.577364,0.577364,-0.577322;2.09444rad)
  shape: bbox 2.54 x 2.799 x 2.54 mm, 23 faces, 0 solids (baked)
FEATURE [Part::Feature] Part__Feature069  label="Pin Header 1x12 TH Pitch 2.54mm015"
  Placement = pos=(6.74521,15.0555,40.428) rot=(0.577364,0.577364,-0.577322;2.09444rad)
  shape: bbox 2.54 x 2.799 x 2.54 mm, 23 faces, 0 solids (baked)
FEATURE [Part::Feature] Part__Feature070  label="Pin Header 1x12 TH Pitch 2.54mm016"
  Placement = pos=(6.74521,15.0555,40.428) rot=(0.577364,0.577364,-0.577322;2.09444rad)
  shape: bbox 2.54 x 2.799 x 2.54 mm, 23 faces, 0 solids (baked)
FEATURE [Part::Feature] Part__Feature071  label="Pin Header 1x12 TH Pitch 2.54mm017"
  Placement = pos=(6.74521,15.0555,40.428) rot=(0.577364,0.577364,-0.577322;2.09444rad)
  shape: bbox 2.54 x 2.799 x 2.54 mm, 23 faces, 0 solids (baked)
FEATURE [Part::Feature] Part__Feature072  label="Pin Header 1x12 TH Pitch 2.54mm018"
  Placement = pos=(6.74521,15.0555,40.428) rot=(0.577364,0.577364,-0.577322;2.09444rad)
  shape: bbox 2.54 x 2.799 x 2.54 mm, 23 faces, 0 solids (baked)
FEATURE [Part::Feature] Part__Feature073  label="Pin Header 1x12 TH Pitch 2.54mm019"
  Placement = pos=(6.74521,15.0555,40.428) rot=(0.577364,0.577364,-0.577322;2.09444rad)
  shape: bbox 2.54 x 2.799 x 2.54 mm, 23 faces, 0 solids (baked)
FEATURE [Part::Feature] Part__Feature074  label="Pin Header 1x12 TH Pitch 2.54mm020"
  Placement = pos=(6.74521,15.0555,40.428) rot=(0.577364,0.577364,-0.577322;2.09444rad)
  shape: bbox 2.54 x 2.799 x 2.54 mm, 23 faces, 0 solids (baked)
FEATURE [Part::Feature] Part__Feature075  label="Pin Header 1x12 TH Pitch 2.54mm021"
  Placement = pos=(6.74521,15.0555,40.428) rot=(0.577364,0.577364,-0.577322;2.09444rad)
  shape: bbox 2.54 x 2.799 x 2.54 mm, 23 faces, 0 solids (baked)
FEATURE [Part::Feature] Part__Feature076  label="Pin Header 1x12 TH Pitch 2.54mm022"
  Placement = pos=(6.74521,15.0555,40.428) rot=(0.577364,0.577364,-0.577322;2.09444rad)
  shape: bbox 2.54 x 2.799 x 2.54 mm, 23 faces, 0 solids (baked)
FEATURE [Part::Feature] Part__Feature077  label="Pin Header 1x12 TH Pitch 2.54mm023"
  Placement = pos=(6.74521,15.0555,40.428) rot=(0.577364,0.577364,-0.577322;2.09444rad)
  shape: bbox 2.54 x 2.799 x 2.54 mm, 23 faces, 0 solids (baked)
FEATURE [App::Part] Pin_Header_1x12_TH_Pitch_2_54mm
  Group = -> [Part__Feature054,Part__Feature055,Part__Feature056,Part__Feature057,Part__Feature058,Part__Feature059,Part__Feature060,Part__Feature061,Part__Feature062,Part__Feature063,Part__Feature064,Part__Feature065,Part__Feature066,Part__Feature067,Part__Feature068,Part__Feature069,Part__Feature070,Part__Feature071,Part__Feature072,Part__Feature073,Part__Feature074,Part__Feature075,Part__Feature076,+1 more]
  License = CC BY 3.0
  LicenseURL = http://creativecommons.org/licenses/by/3.0/
  Origin = -> Origin014
FEATURE [Part::Feature] Part__Feature078  label="Pin Header 1x12 TH Pitch 2.54mm024"
  Placement = pos=(21.9852,15.0555,40.428) rot=(0.577364,0.577364,-0.577322;2.09444rad)
  shape: bbox 0.63 x 12.7 x 0.6305 mm, 14 faces, 0 solids (baked)
FEATURE [Part::Feature] Part__Feature079  label="Pin Header 1x12 TH Pitch 2.54mm025"
  Placement = pos=(21.9852,15.0555,40.428) rot=(0.577364,0.577364,-0.577322;2.09444rad)
  shape: bbox 0.63 x 12.7 x 0.6305 mm, 14 faces, 0 solids (baked)
FEATURE [Part::Feature] Part__Feature080  label="Pin Header 1x12 TH Pitch 2.54mm026"
  Placement = pos=(21.9852,15.0555,40.428) rot=(0.577364,0.577364,-0.577322;2.09444rad)
  shape: bbox 0.63 x 12.7 x 0.6305 mm, 14 faces, 0 solids (baked)
FEATURE [Part::Feature] Part__Feature081  label="Pin Header 1x12 TH Pitch 2.54mm027"
  Placement = pos=(21.9852,15.0555,40.428) rot=(0.577364,0.577364,-0.577322;2.09444rad)
  shape: bbox 0.63 x 12.7 x 0.6305 mm, 14 faces, 0 solids (baked)
FEATURE [Part::Feature] Part__Feature082  label="Pin Header 1x12 TH Pitch 2.54mm028"
  Placement = pos=(21.9852,15.0555,40.428) rot=(0.577364,0.577364,-0.577322;2.09444rad)
  shape: bbox 0.63 x 12.7 x 0.6305 mm, 14 faces, 0 solids (baked)
FEATURE [Part::Feature] Part__Feature083  label="Pin Header 1x12 TH Pitch 2.54mm029"
  Placement = pos=(21.9852,15.0555,40.428) rot=(0.577364,0.577364,-0.577322;2.09444rad)
  shape: bbox 0.63 x 12.7 x 0.6305 mm, 14 faces, 0 solids (baked)
FEATURE [Part::Feature] Part__Feature084  label="Pin Header 1x12 TH Pitch 2.54mm030"
  Placement = pos=(21.9852,15.0555,40.428) rot=(0.577364,0.577364,-0.577322;2.09444rad)
  shape: bbox 0.63 x 12.7 x 0.6305 mm, 14 faces, 0 solids (baked)
FEATURE [Part::Feature] Part__Feature085  label="Pin Header 1x12 TH Pitch 2.54mm031"
  Placement = pos=(21.9852,15.0555,40.428) rot=(0.577364,0.577364,-0.577322;2.09444rad)
  shape: bbox 0.63 x 12.7 x 0.6305 mm, 14 faces, 0 solids (baked)
FEATURE [Part::Feature] Part__Feature086  label="Pin Header 1x12 TH Pitch 2.54mm032"
  Placement = pos=(21.9852,15.0555,40.428) rot=(0.577364,0.577364,-0.577322;2.09444rad)
  shape: bbox 0.63 x 12.7 x 0.6305 mm, 14 faces, 0 solids (baked)
FEATURE [Part::Feature] Part__Feature087  label="Pin Header 1x12 TH Pitch 2.54mm033"
  Placement = pos=(21.9852,15.0555,40.428) rot=(0.577364,0.577364,-0.577322;2.09444rad)
  shape: bbox 0.63 x 12.7 x 0.6305 mm, 14 faces, 0 solids (baked)
FEATURE [Part::Feature] Part__Feature088  label="Pin Header 1x12 TH Pitch 2.54mm034"
  Placement = pos=(21.9852,15.0555,40.428) rot=(0.577364,0.577364,-0.577322;2.09444rad)
  shape: bbox 0.63 x 12.7 x 0.6305 mm, 14 faces, 0 solids (baked)
FEATURE [Part::Feature] Part__Feature089  label="Pin Header 1x12 TH Pitch 2.54mm035"
  Placement = pos=(21.9852,15.0555,40.428) rot=(0.577364,0.577364,-0.577322;2.09444rad)
  shape: bbox 0.63 x 12.7 x 0.6305 mm, 14 faces, 0 solids (baked)
FEATURE [Part::Feature] Part__Feature090  label="Pin Header 1x12 TH Pitch 2.54mm036"
  Placement = pos=(21.9852,15.0555,40.428) rot=(0.577364,0.577364,-0.577322;2.09444rad)
  shape: bbox 2.54 x 2.799 x 2.54 mm, 23 faces, 0 solids (baked)
FEATURE [Part::Feature] Part__Feature091  label="Pin Header 1x12 TH Pitch 2.54mm037"
  Placement = pos=(21.9852,15.0555,40.428) rot=(0.577364,0.577364,-0.577322;2.09444rad)
  shape: bbox 2.54 x 2.799 x 2.54 mm, 23 faces, 0 solids (baked)
FEATURE [Part::Feature] Part__Feature092  label="Pin Header 1x12 TH Pitch 2.54mm038"
  Placement = pos=(21.9852,15.0555,40.428) rot=(0.577364,0.577364,-0.577322;2.09444rad)
  shape: bbox 2.54 x 2.799 x 2.54 mm, 23 faces, 0 solids (baked)
FEATURE [Part::Feature] Part__Feature093  label="Pin Header 1x12 TH Pitch 2.54mm039"
  Placement = pos=(21.9852,15.0555,40.428) rot=(0.577364,0.577364,-0.577322;2.09444rad)
  shape: bbox 2.54 x 2.799 x 2.54 mm, 23 faces, 0 solids (baked)
FEATURE [Part::Feature] Part__Feature094  label="Pin Header 1x12 TH Pitch 2.54mm040"
  Placement = pos=(21.9852,15.0555,40.428) rot=(0.577364,0.577364,-0.577322;2.09444rad)
  shape: bbox 2.54 x 2.799 x 2.54 mm, 23 faces, 0 solids (baked)
FEATURE [Part::Feature] Part__Feature095  label="Pin Header 1x12 TH Pitch 2.54mm041"
  Placement = pos=(21.9852,15.0555,40.428) rot=(0.577364,0.577364,-0.577322;2.09444rad)
  shape: bbox 2.54 x 2.799 x 2.54 mm, 23 faces, 0 solids (baked)
FEATURE [Part::Feature] Part__Feature096  label="Pin Header 1x12 TH Pitch 2.54mm042"
  Placement = pos=(21.9852,15.0555,40.428) rot=(0.577364,0.577364,-0.577322;2.09444rad)
  shape: bbox 2.54 x 2.799 x 2.54 mm, 23 faces, 0 solids (baked)
FEATURE [Part::Feature] Part__Feature097  label="Pin Header 1x12 TH Pitch 2.54mm043"
  Placement = pos=(21.9852,15.0555,40.428) rot=(0.577364,0.577364,-0.577322;2.09444rad)
  shape: bbox 2.54 x 2.799 x 2.54 mm, 23 faces, 0 solids (baked)
FEATURE [Part::Feature] Part__Feature098  label="Pin Header 1x12 TH Pitch 2.54mm044"
  Placement = pos=(21.9852,15.0555,40.428) rot=(0.577364,0.577364,-0.577322;2.09444rad)
  shape: bbox 2.54 x 2.799 x 2.54 mm, 23 faces, 0 solids (baked)
FEATURE [Part::Feature] Part__Feature099  label="Pin Header 1x12 TH Pitch 2.54mm045"
  Placement = pos=(21.9852,15.0555,40.428) rot=(0.577364,0.577364,-0.577322;2.09444rad)
  shape: bbox 2.54 x 2.799 x 2.54 mm, 23 faces, 0 solids (baked)
FEATURE [Part::Feature] Part__Feature100  label="Pin Header 1x12 TH Pitch 2.54mm046"
  Placement = pos=(21.9852,15.0555,40.428) rot=(0.577364,0.577364,-0.577322;2.09444rad)
  shape: bbox 2.54 x 2.799 x 2.54 mm, 23 faces, 0 solids (baked)
FEATURE [Part::Feature] Part__Feature101  label="Pin Header 1x12 TH Pitch 2.54mm047"
  Placement = pos=(21.9852,15.0555,40.428) rot=(0.577364,0.577364,-0.577322;2.09444rad)
  shape: bbox 2.54 x 2.799 x 2.54 mm, 23 faces, 0 solids (baked)
FEATURE [App::Part] Pin_Header_1x12_TH_Pitch_2_54mm001
  Group = -> [Part__Feature078,Part__Feature079,Part__Feature080,Part__Feature081,Part__Feature082,Part__Feature083,Part__Feature084,Part__Feature085,Part__Feature086,Part__Feature087,Part__Feature088,Part__Feature089,Part__Feature090,Part__Feature091,Part__Feature092,Part__Feature093,Part__Feature094,Part__Feature095,Part__Feature096,Part__Feature097,Part__Feature098,Part__Feature099,Part__Feature100,+1 more]
  License = CC BY 3.0
  LicenseURL = http://creativecommons.org/licenses/by/3.0/
  Origin = -> Origin015
FEATURE [Part::Feature] Part__Feature102  label="Pin Header 1x2 TH Pitch 2.54mm"
  Placement = pos=(19.0642,15.0566,31.6645) rot=(0.57735,-0.57735,0.57735;2.0944rad)
  shape: bbox 0.63 x 12.7 x 0.6305 mm, 14 faces, 0 solids (baked)
FEATURE [Part::Feature] Part__Feature103  label="Pin Header 1x2 TH Pitch 2.54mm001"
  Placement = pos=(19.0642,15.0566,31.6645) rot=(0.57735,-0.57735,0.57735;2.0944rad)
  shape: bbox 0.63 x 12.7 x 0.6305 mm, 14 faces, 0 solids (baked)
FEATURE [Part::Feature] Part__Feature104  label="Pin Header 1x2 TH Pitch 2.54mm002"
  Placement = pos=(19.0642,15.0566,31.6645) rot=(0.57735,-0.57735,0.57735;2.0944rad)
  shape: bbox 2.54 x 2.799 x 2.54 mm, 23 faces, 0 solids (baked)
FEATURE [Part::Feature] Part__Feature105  label="Pin Header 1x2 TH Pitch 2.54mm003"
  Placement = pos=(19.0642,15.0566,31.6645) rot=(0.57735,-0.57735,0.57735;2.0944rad)
  shape: bbox 2.54 x 2.799 x 2.54 mm, 23 faces, 0 solids (baked)
FEATURE [App::Part] Pin_Header_1x2_TH_Pitch_2_54mm
  Group = -> [Part__Feature102,Part__Feature103,Part__Feature104,Part__Feature105]
  License = CC BY 3.0
  LicenseURL = http://creativecommons.org/licenses/by/3.0/
  Origin = -> Origin016
FEATURE [Part::Feature] Part__Feature106  label="Pin Header 1x2 TH Pitch 2.54mm004"
  Placement = pos=(19.0642,15.0565,21.2505) rot=(0.577336,-0.577336,0.577379;2.09435rad)
  shape: bbox 0.63 x 12.7 x 0.6305 mm, 14 faces, 0 solids (baked)
FEATURE [Part::Feature] Part__Feature107  label="Pin Header 1x2 TH Pitch 2.54mm005"
  Placement = pos=(19.0642,15.0565,21.2505) rot=(0.577336,-0.577336,0.577379;2.09435rad)
  shape: bbox 0.63 x 12.7 x 0.6305 mm, 14 faces, 0 solids (baked)
FEATURE [Part::Feature] Part__Feature108  label="Pin Header 1x2 TH Pitch 2.54mm006"
  Placement = pos=(19.0642,15.0565,21.2505) rot=(0.577336,-0.577336,0.577379;2.09435rad)
  shape: bbox 2.54 x 2.799 x 2.54 mm, 23 faces, 0 solids (baked)
FEATURE [Part::Feature] Part__Feature109  label="Pin Header 1x2 TH Pitch 2.54mm007"
  Placement = pos=(19.0642,15.0565,21.2505) rot=(0.577336,-0.577336,0.577379;2.09435rad)
  shape: bbox 2.54 x 2.799 x 2.54 mm, 23 faces, 0 solids (baked)
FEATURE [App::Part] Pin_Header_1x2_TH_Pitch_2_54mm001
  Group = -> [Part__Feature106,Part__Feature107,Part__Feature108,Part__Feature109]
  License = CC BY 3.0
  LicenseURL = http://creativecommons.org/licenses/by/3.0/
  Origin = -> Origin017
FEATURE [Part::Feature] Part__Feature110  label="Pin Header 1x6 TH Pitch 2.54mm"
  Placement = pos=(8.01521,15.0566,9.94752) rot=(1,0,0;1.5708rad)
  shape: bbox 0.6305 x 12.7 x 0.63 mm, 14 faces, 0 solids (baked)
FEATURE [Part::Feature] Part__Feature111  label="Pin Header 1x6 TH Pitch 2.54mm001"
  Placement = pos=(8.01521,15.0566,9.94752) rot=(1,0,0;1.5708rad)
  shape: bbox 0.6305 x 12.7 x 0.63 mm, 14 faces, 0 solids (baked)
FEATURE [Part::Feature] Part__Feature112  label="Pin Header 1x6 TH Pitch 2.54mm002"
  Placement = pos=(8.01521,15.0566,9.94752) rot=(1,0,0;1.5708rad)
  shape: bbox 0.6305 x 12.7 x 0.63 mm, 14 faces, 0 solids (baked)
FEATURE [Part::Feature] Part__Feature113  label="Pin Header 1x6 TH Pitch 2.54mm003"
  Placement = pos=(8.01521,15.0566,9.94752) rot=(1,0,0;1.5708rad)
  shape: bbox 0.6305 x 12.7 x 0.63 mm, 14 faces, 0 solids (baked)
FEATURE [Part::Feature] Part__Feature114  label="Pin Header 1x6 TH Pitch 2.54mm004"
  Placement = pos=(8.01521,15.0566,9.94752) rot=(1,0,0;1.5708rad)
  shape: bbox 0.6305 x 12.7 x 0.63 mm, 14 faces, 0 solids (baked)
FEATURE [Part::Feature] Part__Feature115  label="Pin Header 1x6 TH Pitch 2.54mm005"
  Placement = pos=(8.01521,15.0566,9.94752) rot=(1,0,0;1.5708rad)
  shape: bbox 0.6305 x 12.7 x 0.63 mm, 14 faces, 0 solids (baked)
FEATURE [Part::Feature] Part__Feature116  label="Pin Header 1x6 TH Pitch 2.54mm006"
  Placement = pos=(8.01521,15.0566,9.94752) rot=(1,0,0;1.5708rad)
  shape: bbox 2.54 x 2.799 x 2.54 mm, 23 faces, 0 solids (baked)
FEATURE [Part::Feature] Part__Feature117  label="Pin Header 1x6 TH Pitch 2.54mm007"
  Placement = pos=(8.01521,15.0566,9.94752) rot=(1,0,0;1.5708rad)
  shape: bbox 2.54 x 2.799 x 2.54 mm, 23 faces, 0 solids (baked)
FEATURE [Part::Feature] Part__Feature118  label="Pin Header 1x6 TH Pitch 2.54mm008"
  Placement = pos=(8.01521,15.0566,9.94752) rot=(1,0,0;1.5708rad)
  shape: bbox 2.54 x 2.799 x 2.54 mm, 23 faces, 0 solids (baked)
FEATURE [Part::Feature] Part__Feature119  label="Pin Header 1x6 TH Pitch 2.54mm009"
  Placement = pos=(8.01521,15.0566,9.94752) rot=(1,0,0;1.5708rad)
  shape: bbox 2.54 x 2.799 x 2.54 mm, 23 faces, 0 solids (baked)
FEATURE [Part::Feature] Part__Feature120  label="Pin Header 1x6 TH Pitch 2.54mm010"
  Placement = pos=(8.01521,15.0566,9.94752) rot=(1,0,0;1.5708rad)
  shape: bbox 2.54 x 2.799 x 2.54 mm, 23 faces, 0 solids (baked)
FEATURE [Part::Feature] Part__Feature121  label="Pin Header 1x6 TH Pitch 2.54mm011"
  Placement = pos=(8.01521,15.0566,9.94752) rot=(1,0,0;1.5708rad)
  shape: bbox 2.54 x 2.799 x 2.54 mm, 23 faces, 0 solids (baked)
FEATURE [App::Part] Pin_Header_1x6_TH_Pitch_2_54mm
  Group = -> [Part__Feature110,Part__Feature111,Part__Feature112,Part__Feature113,Part__Feature114,Part__Feature115,Part__Feature116,Part__Feature117,Part__Feature118,Part__Feature119,Part__Feature120,Part__Feature121]
  License = CC BY 3.0
  LicenseURL = http://creativecommons.org/licenses/by/3.0/
  Origin = -> Origin018
FEATURE [Part::Feature] Part__Feature122  label="solder"
  Placement = pos=(6.74521,16.7152,40.4275) rot=(0,0,1;0rad)
  shape: bbox 2.042 x 1.62 x 2.042 mm, 8 faces (baked)
FEATURE [Part::Feature] Part__Feature123  label="solder001"
  Placement = pos=(21.9852,16.7152,40.4275) rot=(0,0,1;0rad)
  shape: bbox 2.042 x 1.62 x 2.042 mm, 8 faces (baked)
FEATURE [Part::Feature] Part__Feature124  label="solder002"
  Placement = pos=(19.0642,16.7152,23.7905) rot=(0,0,1;0rad)
  shape: bbox 2.042 x 1.62 x 2.042 mm, 8 faces (baked)
FEATURE [Part::Feature] Part__Feature125  label="solder003"
  Placement = pos=(19.0642,16.7152,34.2045) rot=(0,0,1;0rad)
  shape: bbox 2.042 x 1.62 x 2.042 mm, 8 faces (baked)
FEATURE [Part::Feature] Part__Feature126  label="solder004"
  Placement = pos=(20.7152,16.7152,9.94752) rot=(0,0,1;0rad)
  shape: bbox 2.042 x 1.62 x 2.042 mm, 8 faces (baked)
FEATURE [Part::Feature] Part__Feature127  label="solder005"
  Placement = pos=(6.74521,16.7152,37.8875) rot=(0,0,1;0rad)
  shape: bbox 2.042 x 1.62 x 2.042 mm, 8 faces (baked)
FEATURE [Part::Feature] Part__Feature128  label="solder006"
  Placement = pos=(6.74521,16.7152,35.3475) rot=(0,0,1;0rad)
  shape: bbox 2.042 x 1.62 x 2.042 mm, 8 faces (baked)
FEATURE [Part::Feature] Part__Feature129  label="solder007"
  Placement = pos=(6.74521,16.7152,32.8075) rot=(0,0,1;0rad)
  shape: bbox 2.042 x 1.62 x 2.042 mm, 8 faces (baked)
FEATURE [Part::Feature] Part__Feature130  label="solder008"
  Placement = pos=(6.74521,16.7152,30.2675) rot=(0,0,1;0rad)
  shape: bbox 2.042 x 1.62 x 2.042 mm, 8 faces (baked)
FEATURE [Part::Feature] Part__Feature131  label="solder009"
  Placement = pos=(6.74521,16.7152,27.7275) rot=(0,0,1;0rad)
  shape: bbox 2.042 x 1.62 x 2.042 mm, 8 faces (baked)
FEATURE [Part::Feature] Part__Feature132  label="solder010"
  Placement = pos=(6.74521,16.7152,25.1875) rot=(0,0,1;0rad)
  shape: bbox 2.042 x 1.62 x 2.042 mm, 8 faces (baked)
FEATURE [Part::Feature] Part__Feature133  label="solder011"
  Placement = pos=(6.74521,16.7152,22.6475) rot=(0,0,1;0rad)
  shape: bbox 2.042 x 1.62 x 2.042 mm, 8 faces (baked)
FEATURE [Part::Feature] Part__Feature134  label="solder012"
  Placement = pos=(6.74521,16.7152,20.1075) rot=(0,0,1;0rad)
  shape: bbox 2.042 x 1.62 x 2.042 mm, 8 faces (baked)
FEATURE [Part::Feature] Part__Feature135  label="solder013"
  Placement = pos=(6.74521,16.7152,17.5675) rot=(0,0,1;0rad)
  shape: bbox 2.042 x 1.62 x 2.042 mm, 8 faces (baked)
FEATURE [Part::Feature] Part__Feature136  label="solder014"
  Placement = pos=(6.74521,16.7152,15.0275) rot=(0,0,1;0rad)
  shape: bbox 2.042 x 1.62 x 2.042 mm, 8 faces (baked)
FEATURE [Part::Feature] Part__Feature137  label="solder015"
  Placement = pos=(6.74521,16.7152,12.4875) rot=(0,0,1;0rad)
  shape: bbox 2.042 x 1.62 x 2.042 mm, 8 faces (baked)
FEATURE [Part::Feature] Part__Feature138  label="solder016"
  Placement = pos=(21.9852,16.7152,37.8875) rot=(0,0,1;0rad)
  shape: bbox 2.042 x 1.62 x 2.042 mm, 8 faces (baked)
FEATURE [Part::Feature] Part__Feature139  label="solder017"
  Placement = pos=(21.9852,16.7152,35.3475) rot=(0,0,1;0rad)
  shape: bbox 2.042 x 1.62 x 2.042 mm, 8 faces (baked)
FEATURE [Part::Feature] Part__Feature140  label="solder018"
  Placement = pos=(21.9852,16.7152,32.8075) rot=(0,0,1;0rad)
  shape: bbox 2.042 x 1.62 x 2.042 mm, 8 faces (baked)
FEATURE [Part::Feature] Part__Feature141  label="solder019"
  Placement = pos=(21.9852,16.7152,30.2675) rot=(0,0,1;0rad)
  shape: bbox 2.042 x 1.62 x 2.042 mm, 8 faces (baked)
FEATURE [Part::Feature] Part__Feature142  label="solder020"
  Placement = pos=(21.9852,16.7152,27.7275) rot=(0,0,1;0rad)
  shape: bbox 2.042 x 1.62 x 2.042 mm, 8 faces (baked)
FEATURE [Part::Feature] Part__Feature143  label="solder021"
  Placement = pos=(21.9852,16.7152,25.1875) rot=(0,0,1;0rad)
  shape: bbox 2.042 x 1.62 x 2.042 mm, 8 faces (baked)
FEATURE [Part::Feature] Part__Feature144  label="solder022"
  Placement = pos=(21.9852,16.7152,22.6475) rot=(0,0,1;0rad)
  shape: bbox 2.042 x 1.62 x 2.042 mm, 8 faces (baked)
FEATURE [Part::Feature] Part__Feature145  label="solder023"
  Placement = pos=(21.9852,16.7152,20.1075) rot=(0,0,1;0rad)
  shape: bbox 2.042 x 1.62 x 2.042 mm, 8 faces (baked)
FEATURE [Part::Feature] Part__Feature146  label="solder024"
  Placement = pos=(21.9852,16.7152,17.5675) rot=(0,0,1;0rad)
  shape: bbox 2.042 x 1.62 x 2.042 mm, 8 faces (baked)
FEATURE [Part::Feature] Part__Feature147  label="solder025"
  Placement = pos=(21.9852,16.7152,15.0275) rot=(0,0,1;0rad)
  shape: bbox 2.042 x 1.62 x 2.042 mm, 8 faces (baked)
FEATURE [Part::Feature] Part__Feature148  label="solder026"
  Placement = pos=(21.9852,16.7152,12.4875) rot=(0,0,1;0rad)
  shape: bbox 2.042 x 1.62 x 2.042 mm, 8 faces (baked)
FEATURE [Part::Feature] Part__Feature149  label="solder027"
  Placement = pos=(19.0642,16.7152,21.2505) rot=(0,0,1;0rad)
  shape: bbox 2.042 x 1.62 x 2.042 mm, 8 faces (baked)
FEATURE [Part::Feature] Part__Feature150  label="solder028"
  Placement = pos=(19.0642,16.7152,31.6645) rot=(0,0,1;0rad)
  shape: bbox 2.042 x 1.62 x 2.042 mm, 8 faces (baked)
FEATURE [Part::Feature] Part__Feature151  label="solder029"
  Placement = pos=(18.1752,16.7152,9.94752) rot=(0,0,1;0rad)
  shape: bbox 2.042 x 1.62 x 2.042 mm, 8 faces (baked)
FEATURE [Part::Feature] Part__Feature152  label="solder030"
  Placement = pos=(15.6352,16.7152,9.94752) rot=(0,0,1;0rad)
  shape: bbox 2.042 x 1.62 x 2.042 mm, 8 faces (baked)
FEATURE [Part::Feature] Part__Feature153  label="solder031"
  Placement = pos=(13.0952,16.7152,9.94752) rot=(0,0,1;0rad)
  shape: bbox 2.042 x 1.62 x 2.042 mm, 8 faces (baked)
FEATURE [Part::Feature] Part__Feature154  label="solder032"
  Placement = pos=(10.5552,16.7152,9.94752) rot=(0,0,1;0rad)
  shape: bbox 2.042 x 1.62 x 2.042 mm, 8 faces (baked)
FEATURE [Part::Feature] Part__Feature155  label="solder033"
  Placement = pos=(8.01521,16.7152,9.94752) rot=(0,0,1;0rad)
  shape: bbox 2.042 x 1.62 x 2.042 mm, 8 faces (baked)
FEATURE [App::Part] ASSEMBLY  label="Arduino Mini Pro"
  Group = -> [Part__Feature003,Part__Feature004,cap_603,cap_603001,cap_603002,cap_603003,res_603,res_603001,res_603002,condensateurTantale_106C_D__faut,condensateurTantale_106C_D__faut001,SOT23_5,Surface_Mount_Chip_LED_3_2x1_6mm,Surface_Mount_Chip_LED_3_2x1_6mm001,Crystal_Low_Profile,Part__Feature053,Pin_Header_1x12_TH_Pitch_2_54mm,Pin_Header_1x12_TH_Pitch_2_54mm001,Pin_Header_1x2_TH_Pitch_2_54mm,+36 more]
  License = CC BY 3.0
  LicenseURL = http://creativecommons.org/licenses/by/3.0/
  Origin = -> Origin019
  Placement = pos=(14.3075,-32.235,21) rot=(0,-1,0;-3.14159rad)
FEATURE [Part::Box] Box002  label="PCB"
  AttacherType = Attacher::AttachEngine3D
  Height = 36
  Length = 30
  Placement = pos=(-15,-26,-22) rot=(0,0,1;0rad)
  Width = 1.5
FEATURE [Part::Chamfer] Chamfer002  label="M3 10mm001"
  Edges = 2 edges r=0.1: [Edge6,Edge7]
  Placement = pos=(0,30,16) rot=(0,0,1;0rad)
FEATURE [Part::Chamfer] Chamfer003  label="M3 10mm002"
  Edges = 2 edges r=0.1: [Edge6,Edge7]
  Placement = pos=(30,0,16) rot=(0,0,1;0rad)
FEATURE [Part::Chamfer] Chamfer004  label="M3 10mm003"
  Edges = 2 edges r=0.1: [Edge6,Edge7]
  Placement = pos=(-30,0,16) rot=(0,0,1;0rad)
FEATURE [App::DocumentObjectGroup] Group  label="M3 10mm"
  Group = -> [Chamfer002,Chamfer003,Chamfer004,Chamfer001]
FEATURE [Part::Chamfer] Chamfer  label="parte inferior002"
  Base = -> Cut019
  Edges = 8 edges r=1: [Edge39,Edge41,Edge42,Edge45,Edge47,Edge50,Edge52,Edge57]
FEATURE [Part::Cylinder] Cylinder062  label="orificio entrada cables inf001"
  Angle = 10
  AttacherType = Attacher::AttachEngine3D
  Height = 8
  Placement = pos=(0,0,-13) rot=(0,0,1;1.0821rad)
  Radius = 41.5
FEATURE [Part::Cylinder] Cylinder063  label="orificio entrada cables inf002"
  Angle = 10
  AttacherType = Attacher::AttachEngine3D
  Height = 15
  Placement = pos=(0,0,-13) rot=(0,0,1;1.0821rad)
  Radius = 39.8
FEATURE [Part::Cut] Cut021  label="tapa entrada tira led inf"
  Base = -> Cylinder062
  Tool = -> Cylinder063
FEATURE [Part::Cylinder] Cylinder064  label="orificio entrada cables inf003"
  Angle = 10
  AttacherType = Attacher::AttachEngine3D
  Height = 8
  Placement = pos=(0,0,-13) rot=(0,0,1;1.0821rad)
  Radius = 41.5
FEATURE [Part::Cylinder] Cylinder065  label="orificio entrada cables inf004"
  Angle = 10
  AttacherType = Attacher::AttachEngine3D
  Height = 15
  Placement = pos=(0,0,-13) rot=(0,0,1;1.0821rad)
  Radius = 39.8
FEATURE [Part::Cut] Cut022  label="tapa entrada tira led sup"
  Base = -> Cylinder064
  Placement = pos=(0,0,8) rot=(0,0,1;0rad)
  Tool = -> Cylinder065
FEATURE [Part::MultiFuse] Fusion038  label="parte superior "
  Shapes = -> [Cut020,Cut022]
FEATURE [Part::MultiFuse] Fusion039  label="parte inferior003"
  Shapes = -> [Chamfer,Cut021]
FEATURE [Part::Chamfer] Chamfer005  label="parte superior OK"
  Base = -> Fusion038
  Edges = 1 edges r=1.4: [Edge119]
FEATURE [Part::Chamfer] Chamfer006  label="parte inferior OK"
  Base = -> Fusion039
  Edges = 1 edges r=1.4: [Edge117]
FEATURE [Part::Feature] Fillet006  label="button-body"
  shape: bbox 6.2 x 6.2 x 5.2 mm, 41 faces (baked)
FEATURE [Part::Feature] Pad003004  label="top-metal-plate001"
  Placement = pos=(0,0,3.2) rot=(0,0,1;0rad)
  shape: bbox 6.2 x 6.2 x 0.2 mm, 15 faces (baked)
FEATURE [Part::Feature] Fillet002  label="pin-002"
  Placement = pos=(-3.2,2.8,0) rot=(1,0,0;1.5708rad)
  shape: bbox 0.922 x 0.7 x 4.6 mm, 20 faces (baked)
FEATURE [Part::Feature] Fillet003  label="pin-003"
  Placement = pos=(3.2,-2.8,0) rot=(0,0.707107,0.707107;-3.14159rad)
  shape: bbox 0.922 x 0.7 x 4.6 mm, 20 faces (baked)
FEATURE [Part::Feature] Fillet001  label="pin-1"
  Placement = pos=(-3.2,-2.2,0) rot=(1,0,0;1.5708rad)
  shape: bbox 0.922 x 0.7 x 4.6 mm, 20 faces (baked)
FEATURE [Part::Feature] Fillet004  label="pin-004"
  Placement = pos=(3.2,2.2,0) rot=(0,0.707107,0.707107;-3.14159rad)
  shape: bbox 0.922 x 0.7 x 4.6 mm, 20 faces (baked)
FEATURE [Part::Compound] Compound  label="pushbutton-mini"
  Links = -> [Fillet006,Fillet003,Fillet001,Fillet002,Fillet004,Pad003004]
  Placement = pos=(0,16,15) rot=(0,0,1;0rad)
FEATURE [App::DocumentObjectGroup] Group001  label="Componentes"
  Group = -> [Small_Toggle_Switch,Fusion019,Part__Feature,ASSEMBLY,Box002,Compound]
FEATURE [Part::Box] Box  label="Cubo"
  AttacherType = Attacher::AttachEngine3D
  Height = 6
  Length = 7
  Placement = pos=(-3.5,12.5,12.5) rot=(0,0,1;0rad)
  Width = 7
FEATURE [Part::Cylinder] Cylinder066  label="Cilindro"
  Angle = 360
  AttacherType = Attacher::AttachEngine3D
  Height = 10
  Placement = pos=(0,16,10) rot=(0,0,1;0rad)
  Radius = 1.8
FEATURE [Part::MultiFuse] Fusion040  label="vaciado mini pushbutton"
  Shapes = -> [Box,Cylinder066]
FEATURE [Part::Cut] Cut023  label="tapa con pushbutton mini"
  Base = -> Cut008
  Tool = -> Fusion040
